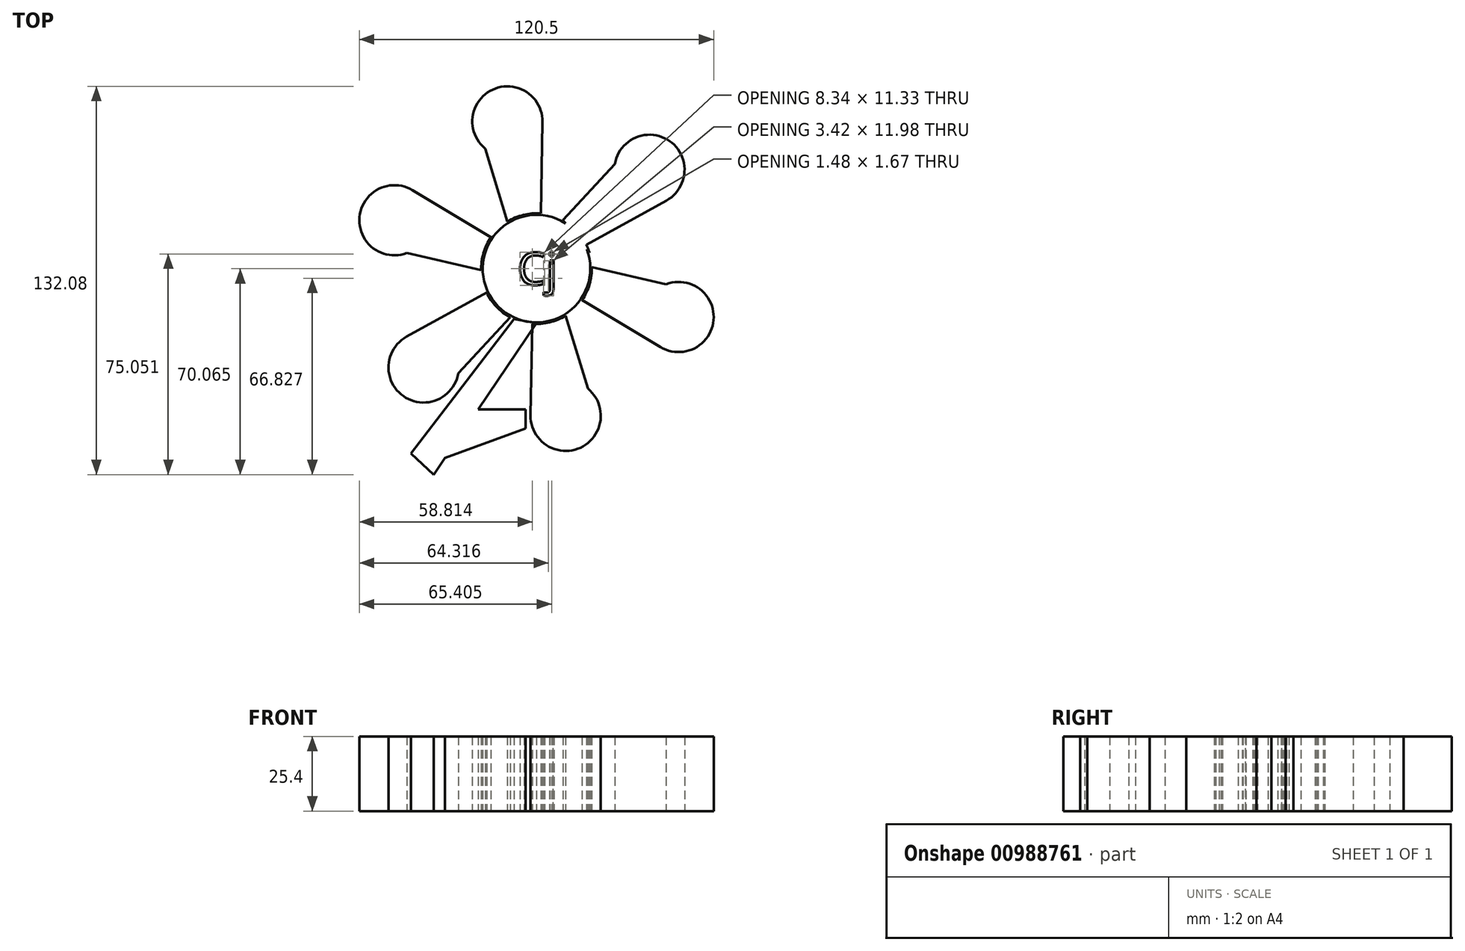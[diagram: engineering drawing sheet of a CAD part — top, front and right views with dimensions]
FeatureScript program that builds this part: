
annotation { "Feature Type Name" : "Feature", "Feature Type Description" : "" }
export const myFeature = defineFeature(function(context is Context, id is Id, definition is map)
    precondition{}
    {
        {
            var Q0;
            Q0=qCreatedBy(makeId("Top.planeOp"),FACE);
            var sketch = newSketch(context, id + "F0", { "sketchPlane" : qUnion([Q0])});
            skCircle(sketch, "E0", {"center": v(0, 0) * mm, "radius": 18.8 * mm});
            skLineSegment(sketch, "E1", {"start": v(8.92, 16.56) * mm, "end": v(26.62, 35.54) * mm});
            skArc(sketch, "E2", {"start": v(44.18, 23.17) * mm, "mid": v(45.28, 43.37) * mm, "end": v(26.62, 35.54) * mm});
            skLineSegment(sketch, "E3", {"start": v(44.18, 23.17) * mm, "end": v(16.97, 8.12) * mm});
            skLineSegment(sketch, "E4", {"start": v(8.92, 16.56) * mm, "end": v(18, 5.44) * mm});
            skLineSegment(sketch, "E5.1.0", {"start": v(-9.88, 16) * mm, "end": v(-17.47, 40.83) * mm});
            skArc(sketch, "E5.1.1", {"start": v(2.02, 49.84) * mm, "mid": v(-14.92, 60.9) * mm, "end": v(-17.47, 40.83) * mm});
            skLineSegment(sketch, "E5.1.2", {"start": v(2.02, 49.84) * mm, "end": v(1.46, 18.75) * mm});
            skLineSegment(sketch, "E5.2.0", {"start": v(-18.8, -0.55) * mm, "end": v(-44.1, 5.28) * mm});
            skArc(sketch, "E5.2.1", {"start": v(-42.15, 26.68) * mm, "mid": v(-60.2, 17.53) * mm, "end": v(-44.1, 5.28) * mm});
            skLineSegment(sketch, "E5.2.2", {"start": v(-42.15, 26.68) * mm, "end": v(-15.51, 10.64) * mm});
            skLineSegment(sketch, "E5.3.0", {"start": v(-8.92, -16.56) * mm, "end": v(-26.62, -35.54) * mm});
            skArc(sketch, "E5.3.1", {"start": v(-44.18, -23.17) * mm, "mid": v(-45.28, -43.37) * mm, "end": v(-26.62, -35.54) * mm});
            skLineSegment(sketch, "E5.3.2", {"start": v(-44.18, -23.17) * mm, "end": v(-16.97, -8.12) * mm});
            skLineSegment(sketch, "E5.4.0", {"start": v(9.88, -16) * mm, "end": v(17.47, -40.83) * mm});
            skArc(sketch, "E5.4.1", {"start": v(-2.02, -49.84) * mm, "mid": v(14.92, -60.9) * mm, "end": v(17.47, -40.83) * mm});
            skLineSegment(sketch, "E5.4.2", {"start": v(-2.02, -49.84) * mm, "end": v(-1.46, -18.75) * mm});
            skLineSegment(sketch, "E5.5.0", {"start": v(18.8, 0.55) * mm, "end": v(44.1, -5.28) * mm});
            skArc(sketch, "E5.5.1", {"start": v(42.15, -26.68) * mm, "mid": v(60.2, -17.53) * mm, "end": v(44.1, -5.28) * mm});
            skLineSegment(sketch, "E5.5.2", {"start": v(42.15, -26.68) * mm, "end": v(15.51, -10.64) * mm});
            skSolve(sketch);
        }
        {
            var Q0;
            {var subQ0=sQuery(id+"F0.wireOp",EDGE,"E1");Q0=makeQuery(id+"F0.imprint","IMPRINT",FACE,{"disambiguationData":[TD([[makeQuery(id+"F0.imprint","IMPRINT",EDGE,{"derivedFrom":subQ0}),-1.0]])]});}
            var Q1;
            {var subQ0=sQuery(id+"F0.wireOp",EDGE,"E5.2.0");Q1=makeQuery(id+"F0.imprint","IMPRINT",FACE,{"disambiguationData":[TD([[makeQuery(id+"F0.imprint","IMPRINT",EDGE,{"derivedFrom":subQ0}),-1.0]])]});}
            var Q2;
            {var subQ0=sQuery(id+"F0.wireOp",EDGE,"E5.3.0");Q2=makeQuery(id+"F0.imprint","IMPRINT",FACE,{"disambiguationData":[TD([[makeQuery(id+"F0.imprint","IMPRINT",EDGE,{"derivedFrom":subQ0}),-1.0]])]});}
            var Q3;
            {var subQ0=sQuery(id+"F0.wireOp",EDGE,"E5.4.0");Q3=makeQuery(id+"F0.imprint","IMPRINT",FACE,{"disambiguationData":[TD([[makeQuery(id+"F0.imprint","IMPRINT",EDGE,{"derivedFrom":subQ0}),-1.0]])]});}
            var Q4;
            {var subQ0=sQuery(id+"F0.wireOp",EDGE,"E5.5.0");Q4=makeQuery(id+"F0.imprint","IMPRINT",FACE,{"disambiguationData":[TD([[makeQuery(id+"F0.imprint","IMPRINT",EDGE,{"derivedFrom":subQ0}),-1.0]])]});}
            var Q5;
            {var subQ2=sQuery(id+"F0.wireOp",EDGE,"E4");Q5=makeQuery(id+"F0.imprint","IMPRINT",FACE,{"disambiguationData":[TD([[makeQuery(id+"F0.imprint","IMPRINT",EDGE,{"derivedFrom":subQ2}),1.0]])]});}
            var Q6;
            {var subQ0=sQuery(id+"F0.wireOp",EDGE,"E5.1.0");Q6=makeQuery(id+"F0.imprint","IMPRINT",FACE,{"disambiguationData":[TD([[makeQuery(id+"F0.imprint","IMPRINT",EDGE,{"derivedFrom":subQ0}),-1.0]])]});}
            extrude(context, id + "F1", {"entities" : qUnion([Q0, Q1, Q2, Q3, Q4, Q5, Q6]), "depth" : 25.4 * mm, "offsetDistance" : 25.4 * mm});
        }
        {
            var Q0;
            Q0=qCreatedBy(makeId("Top.planeOp"),FACE);
            var sketch = newSketch(context, id + "F2", { "sketchPlane" : qUnion([Q0])});
            skCircle(sketch, "E6", {"center": v(0, 0) * mm, "radius": 18.3 * mm});
            skText(sketch, "E7", { "text": "Cj\n", "fontName": "OpenSans-Regular.ttf"});
            const initialGuessF2  = {"E7": [-0.00655, -0.00553, 1, 0, 0.01112]};
            skSetInitialGuess(sketch, initialGuessF2);
            skSolve(sketch);
        }
        {
            var Q0;
            Q0 = qSketchRegion(id + "F2", true);
            extrude(context, id + "F3", {"entities" : qUnion([Q0]), "operationType" : NewBodyOperationType.ADD, "depth" : 25.4 * mm, "offsetDistance" : 25.4 * mm});
        }
        {
            var Q0;
            Q0=qCreatedBy(makeId("Top.planeOp"),FACE);
            var sketch = newSketch(context, id + "F4", { "sketchPlane" : qUnion([Q0])});
            skLineSegment(sketch, "E8", {"start": v(-7.63, -17.12) * mm, "end": v(-42.74, -62.89) * mm});
            skLineSegment(sketch, "E9", {"start": v(0, -18.56) * mm, "end": v(-34.97, -70.08) * mm});
            skLineSegment(sketch, "E10", {"start": v(-42.74, -62.89) * mm, "end": v(-34.97, -70.08) * mm});
            skLineSegment(sketch, "E11", {"start": v(-7.63, -17.12) * mm, "end": v(0, -18.56) * mm});
            skLineSegment(sketch, "E12", {"start": v(-31.1, -64.37) * mm, "end": v(-3.76, -54.38) * mm});
            skLineSegment(sketch, "E13", {"start": v(-3.76, -54.38) * mm, "end": v(-3.76, -47.87) * mm});
            skLineSegment(sketch, "E14", {"start": v(-3.55, -47.87) * mm, "end": v(-19.9, -47.87) * mm});
            skSolve(sketch);
        }
        {
            var Q0;
            Q0 = qSketchRegion(id + "F4", true);
            extrude(context, id + "F5", {"entities" : qUnion([Q0]), "depth" : 25.4 * mm, "offsetDistance" : 25.4 * mm});
        }
    });
